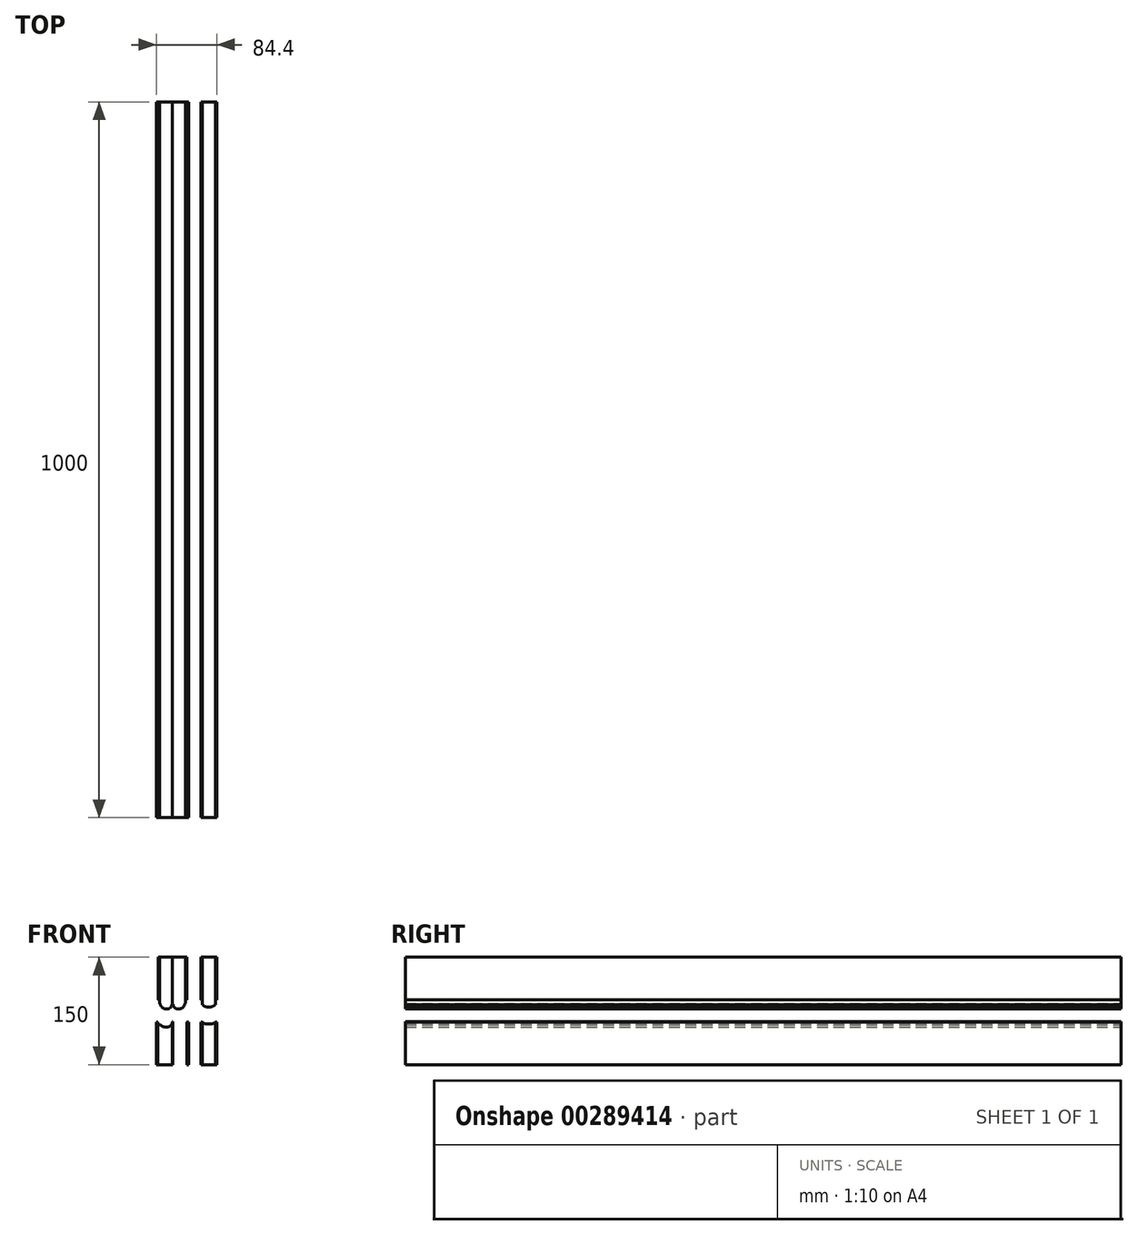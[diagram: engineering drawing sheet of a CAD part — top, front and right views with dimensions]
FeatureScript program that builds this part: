
annotation { "Feature Type Name" : "Feature", "Feature Type Description" : "" }
export const myFeature = defineFeature(function(context is Context, id is Id, definition is map)
    precondition{}
    {
        {
            assignVariable(context, id + "F0", {"name" : "lProfil", "anyValue" : 1000});
        }
        {
            var Q0;
            Q0=qCreatedBy(makeId("Front.planeOp"),FACE);
            var sketch = newSketch(context, id + "F1", { "sketchPlane" : qUnion([Q0])});
            skLineSegment(sketch, "E0.bottom", {"start": v(-18, 72.21) * mm, "end": v(0, 72.21) * mm});
            skLineSegment(sketch, "E0.top", {"start": v(-9.3, 0) * mm, "end": v(-7.3, 0) * mm});
            skLineSegment(sketch, "E0.left", {"start": v(-18, 72.21) * mm, "end": v(-18, 8) * mm});
            skLineSegment(sketch, "E0.right", {"start": v(0, 72.21) * mm, "end": v(0, 6.3) * mm});
            skPoint(sketch, "E1.visualSharp", {"position": v(0, 0) * mm});
            skArc(sketch, "E1.filletArc", {"start": v(-7.3, 0) * mm, "mid": v(-2.85, 1.85) * mm, "end": v(-1, 6.3) * mm});
            skPoint(sketch, "E2.visualSharp", {"position": v(-18, 0) * mm});
            skArc(sketch, "E2.filletArc", {"start": v(-17.3, 8) * mm, "mid": v(-14.96, 2.34) * mm, "end": v(-9.3, 0) * mm});
            skLineSegment(sketch, "E3", {"start": v(0, 6.3) * mm, "end": v(-1, 6.3) * mm});
            skLineSegment(sketch, "E4", {"start": v(-18, 8) * mm, "end": v(-17.3, 8) * mm});
            skLineSegment(sketch, "E5.MirrorCS", {"start": v(18, 72.21) * mm, "end": v(0, 72.21) * mm});
            skLineSegment(sketch, "E6.MirrorCS", {"start": v(18, 72.21) * mm, "end": v(18, 8) * mm});
            skLineSegment(sketch, "E7.MirrorCS", {"start": v(18, 8) * mm, "end": v(17.3, 8) * mm});
            skArc(sketch, "E8.MirrorCS", {"start": v(17.3, 8) * mm, "mid": v(14.96, 2.34) * mm, "end": v(9.3, 0) * mm});
            skLineSegment(sketch, "E9.MirrorCS", {"start": v(9.3, 0) * mm, "end": v(7.3, 0) * mm});
            skArc(sketch, "E10.MirrorCS", {"start": v(7.3, 0) * mm, "mid": v(2.85, 1.85) * mm, "end": v(1, 6.3) * mm});
            skLineSegment(sketch, "E11.MirrorCS", {"start": v(0, 6.3) * mm, "end": v(1, 6.3) * mm});
            skLineSegment(sketch, "E12.bottom", {"start": v(-0.4, -17.79) * mm, "end": v(0.4, -17.79) * mm});
            skLineSegment(sketch, "E12.top", {"start": v(-0.4, -77.79) * mm, "end": v(0.4, -77.79) * mm});
            skLineSegment(sketch, "E12.left", {"start": v(-0.4, -17.79) * mm, "end": v(-0.4, -77.79) * mm});
            skLineSegment(sketch, "E12.right", {"start": v(0.4, -17.79) * mm, "end": v(0.4, -77.79) * mm});
            skLineSegment(sketch, "E13", {"start": v(0, 0) * mm, "end": v(0, 6.3) * mm, "construction": true});
            skLineSegment(sketch, "E14", {"start": v(-10.7, -25.09) * mm, "end": v(-6.7, -25.09) * mm});
            skArc(sketch, "E15", {"start": v(-6.7, -25.09) * mm, "mid": v(-2.25, -23.24) * mm, "end": v(-0.4, -18.79) * mm});
            skArc(sketch, "E16", {"start": v(-10.7, -25.09) * mm, "mid": v(-13.96, -24.4) * mm, "end": v(-16.66, -22.43) * mm});
            skLineSegment(sketch, "E17", {"start": v(-16.66, -22.43) * mm, "end": v(-20.4, -22.43) * mm});
            skLineSegment(sketch, "E18", {"start": v(-20.4, -77.79) * mm, "end": v(-0.4, -77.79) * mm});
            skLineSegment(sketch, "E19", {"start": v(-18, 8) * mm, "end": v(-16.66, 4.86) * mm, "construction": true});
            skArc(sketch, "E20.MirrorCS", {"start": v(6.7, -25.09) * mm, "mid": v(2.25, -23.24) * mm, "end": v(0.4, -18.79) * mm});
            skLineSegment(sketch, "E21.MirrorCS", {"start": v(10.7, -25.09) * mm, "end": v(6.7, -25.09) * mm});
            skArc(sketch, "E22.MirrorCS", {"start": v(10.7, -25.09) * mm, "mid": v(13.96, -24.4) * mm, "end": v(16.66, -22.43) * mm});
            skLineSegment(sketch, "E23.MirrorCS", {"start": v(16.66, -22.43) * mm, "end": v(20.4, -22.43) * mm});
            skLineSegment(sketch, "E24.MirrorCS", {"start": v(20.4, -22.43) * mm, "end": v(20.4, -77.79) * mm});
            skLineSegment(sketch, "E25.MirrorCS", {"start": v(20.4, -77.79) * mm, "end": v(0.4, -77.79) * mm});
            skLineSegment(sketch, "E26.bottom", {"start": v(-20.4, -77.79) * mm, "end": v(-22.4, -77.79) * mm});
            skLineSegment(sketch, "E26.top", {"start": v(-20.9, -18.25) * mm, "end": v(-22.4, -18.25) * mm});
            skLineSegment(sketch, "E26.left", {"start": v(-20.4, -77.79) * mm, "end": v(-20.4, -18.75) * mm});
            skLineSegment(sketch, "E26.right", {"start": v(-22.4, -77.79) * mm, "end": v(-22.4, -18.25) * mm});
            skLineSegment(sketch, "E27", {"start": v(-20.4, -18.25) * mm, "end": v(-16.66, -22.43) * mm, "construction": true});
            skPoint(sketch, "E28.visualSharp", {"position": v(-20.4, -18.25) * mm});
            skArc(sketch, "E28.filletArc", {"start": v(-20.4, -18.75) * mm, "mid": v(-20.55, -18.4) * mm, "end": v(-20.9, -18.25) * mm});
            skLineSegment(sketch, "E29.MirrorCS", {"start": v(22.4, -77.79) * mm, "end": v(22.4, -18.25) * mm});
            skLineSegment(sketch, "E30.MirrorCS", {"start": v(20.4, -77.79) * mm, "end": v(22.4, -77.79) * mm});
            skLineSegment(sketch, "E31.MirrorCS", {"start": v(20.9, -18.25) * mm, "end": v(22.4, -18.25) * mm});
            skLineSegment(sketch, "E32.MirrorCS", {"start": v(20.4, -77.79) * mm, "end": v(20.4, -18.75) * mm});
            skArc(sketch, "E33.MirrorCS", {"start": v(20.4, -18.75) * mm, "mid": v(20.55, -18.4) * mm, "end": v(20.9, -18.25) * mm});
            skLineSegment(sketch, "E34.bottom", {"start": v(-18, 72.21) * mm, "end": v(-20, 72.21) * mm});
            skLineSegment(sketch, "E34.top", {"start": v(-18, 12.68) * mm, "end": v(-19.5, 12.68) * mm});
            skLineSegment(sketch, "E34.right", {"start": v(-20, 72.21) * mm, "end": v(-20, 13.18) * mm});
            skPoint(sketch, "E35.visualSharp", {"position": v(-20, 12.68) * mm});
            skArc(sketch, "E35.filletArc", {"start": v(-20, 13.18) * mm, "mid": v(-19.85, 12.83) * mm, "end": v(-19.5, 12.68) * mm});
            skLineSegment(sketch, "E36.MirrorCS", {"start": v(18, 12.68) * mm, "end": v(19.5, 12.68) * mm});
            skArc(sketch, "E37.MirrorCS", {"start": v(20, 13.18) * mm, "mid": v(19.85, 12.83) * mm, "end": v(19.5, 12.68) * mm});
            skLineSegment(sketch, "E38.MirrorCS", {"start": v(20, 72.21) * mm, "end": v(20, 13.18) * mm});
            skLineSegment(sketch, "E39.MirrorCS", {"start": v(18, 72.21) * mm, "end": v(20, 72.21) * mm});
            skLineSegment(sketch, "E40.bottom", {"start": v(42, 72.21) * mm, "end": v(60, 72.21) * mm});
            skLineSegment(sketch, "E40.left", {"start": v(42, 72.21) * mm, "end": v(42, 6) * mm});
            skLineSegment(sketch, "E40.right", {"start": v(60, 72.21) * mm, "end": v(60, 6.08) * mm});
            skLineSegment(sketch, "E41", {"start": v(49.28, 2.62) * mm, "end": v(51.28, 2.62) * mm});
            skArc(sketch, "E42", {"start": v(51.28, 2.62) * mm, "mid": v(55.97, 3.52) * mm, "end": v(60, 6.08) * mm});
            skArc(sketch, "E43", {"start": v(49.28, 2.62) * mm, "mid": v(45.27, 3.5) * mm, "end": v(42, 6) * mm});
            skLineSegment(sketch, "E44", {"start": v(30, 72.21) * mm, "end": v(30, 0) * mm, "construction": true});
            skLineSegment(sketch, "E45.MirrorCS", {"start": v(40, 72.21) * mm, "end": v(40, 13.18) * mm});
            skLineSegment(sketch, "E46.MirrorCS", {"start": v(42, 12.68) * mm, "end": v(40.5, 12.68) * mm});
            skArc(sketch, "E47.MirrorCS", {"start": v(40, 13.18) * mm, "mid": v(40.15, 12.83) * mm, "end": v(40.5, 12.68) * mm});
            skLineSegment(sketch, "E48.MirrorCS", {"start": v(42, 72.21) * mm, "end": v(40, 72.21) * mm});
            skLineSegment(sketch, "E49", {"start": v(51, 72.21) * mm, "end": v(51, 2.62) * mm, "construction": true});
            skLineSegment(sketch, "E50.MirrorCS", {"start": v(62, 72.21) * mm, "end": v(62, 13.18) * mm});
            skLineSegment(sketch, "E51.MirrorCS", {"start": v(60, 12.68) * mm, "end": v(61.5, 12.68) * mm});
            skArc(sketch, "E52.MirrorCS", {"start": v(62, 13.18) * mm, "mid": v(61.85, 12.83) * mm, "end": v(61.5, 12.68) * mm});
            skLineSegment(sketch, "E53.MirrorCS", {"start": v(60, 72.21) * mm, "end": v(62, 72.21) * mm});
            skLineSegment(sketch, "E54.MirrorCS", {"start": v(42, -77.79) * mm, "end": v(42, -18.75) * mm});
            skLineSegment(sketch, "E55.MirrorCS", {"start": v(40, -77.79) * mm, "end": v(40, -18.25) * mm});
            skLineSegment(sketch, "E56.MirrorCS", {"start": v(41.5, -18.25) * mm, "end": v(40, -18.25) * mm});
            skArc(sketch, "E57.MirrorCS", {"start": v(42, -18.75) * mm, "mid": v(41.85, -18.4) * mm, "end": v(41.5, -18.25) * mm});
            skLineSegment(sketch, "E58.MirrorCS", {"start": v(42, -77.79) * mm, "end": v(40, -77.79) * mm});
            skLineSegment(sketch, "E59.MirrorCS", {"start": v(60, -77.79) * mm, "end": v(60, -18.75) * mm});
            skLineSegment(sketch, "E60.MirrorCS", {"start": v(62, -77.79) * mm, "end": v(62, -18.25) * mm});
            skLineSegment(sketch, "E61.MirrorCS", {"start": v(60.5, -18.25) * mm, "end": v(62, -18.25) * mm});
            skArc(sketch, "E62.MirrorCS", {"start": v(60, -18.75) * mm, "mid": v(60.15, -18.4) * mm, "end": v(60.5, -18.25) * mm});
            skLineSegment(sketch, "E63.MirrorCS", {"start": v(60, -77.79) * mm, "end": v(62, -77.79) * mm});
            skLineSegment(sketch, "E64", {"start": v(42, -77.79) * mm, "end": v(60, -77.79) * mm});
            skLineSegment(sketch, "E65", {"start": v(48.28, -21.12) * mm, "end": v(52.28, -21.12) * mm});
            skArc(sketch, "E66", {"start": v(52.28, -21.12) * mm, "mid": v(56.16, -20.51) * mm, "end": v(59.67, -18.75) * mm});
            skArc(sketch, "E67", {"start": v(48.28, -21.12) * mm, "mid": v(44.93, -20.5) * mm, "end": v(42, -18.75) * mm});
            skLineSegment(sketch, "E68", {"start": v(50.28, 2.62) * mm, "end": v(50.28, -21.12) * mm, "construction": true});
            skLineSegment(sketch, "E69", {"start": v(60, -18.75) * mm, "end": v(59.67, -18.75) * mm});
            skSolve(sketch);
        }
        {
            var Q0;
            Q0=makeQuery(id+"F1.imprint","IMPRINT",FACE,{"disambiguationData":[TD([[makeQuery(id+"F1.imprint","IMPRINT",EDGE,{"derivedFrom":sQuery(id+"F1.wireOp",EDGE,"E0.bottom")}),-1.0]])]});
            var Q1;
            Q1=makeQuery(id+"F1.imprint","IMPRINT",FACE,{"disambiguationData":[TD([[makeQuery(id+"F1.imprint","IMPRINT",EDGE,{"derivedFrom":sQuery(id+"F1.wireOp",EDGE,"E14")}),-1.0]])]});
            var Q2;
            {var subQ1=sQuery(id+"F1.wireOp",EDGE,"E40.bottom");Q2=makeQuery(id+"F1.imprint","IMPRINT",FACE,{"disambiguationData":[TD([[makeQuery(id+"F1.imprint","IMPRINT",EDGE,{"derivedFrom":subQ1}),-1.0]])]});}
            var Q3;
            Q3=makeQuery(id+"F1.imprint","IMPRINT",FACE,{"disambiguationData":[TD([[makeQuery(id+"F1.imprint","IMPRINT",EDGE,{"derivedFrom":sQuery(id+"F1.wireOp",EDGE,"E54.MirrorCS")}),-1.0]])]});
            extrude(context, id + "F2", {"entities" : qUnion([Q0, Q1, Q2, Q3]), "depth" : (getVariable(context, 'lProfil')) * mm});
        }
        {
            var Q0;
            {var subQ0=sQuery(id+"F1.wireOp",EDGE,"E20.MirrorCS");Q0=makeQuery(id+"F1.imprint","IMPRINT",FACE,{"disambiguationData":[TD([[makeQuery(id+"F1.imprint","IMPRINT",EDGE,{"derivedFrom":subQ0}),1.0]])]});}
            var Q1;
            Q1=makeQuery(id+"F1.imprint","IMPRINT",FACE,{"disambiguationData":[TD([[makeQuery(id+"F1.imprint","IMPRINT",EDGE,{"derivedFrom":sQuery(id+"F1.wireOp",EDGE,"E0.right")}),1.0]])]});
            extrude(context, id + "F3", {"entities" : qUnion([Q0, Q1]), "depth" : (getVariable(context, 'lProfil')) * mm});
        }
        {
            var Q0;
            {var subQ3=sQuery(id+"F1.wireOp",EDGE,"E26.bottom");Q0=makeQuery(id+"F1.imprint","IMPRINT",FACE,{"disambiguationData":[TD([[makeQuery(id+"F1.imprint","IMPRINT",EDGE,{"derivedFrom":subQ3}),-1.0]])]});}
            var Q1;
            {var subQ3=sQuery(id+"F1.wireOp",EDGE,"E12.bottom");Q1=makeQuery(id+"F1.imprint","IMPRINT",FACE,{"disambiguationData":[TD([[makeQuery(id+"F1.imprint","IMPRINT",EDGE,{"derivedFrom":subQ3}),-1.0]])]});}
            var Q2;
            Q2=makeQuery(id+"F1.imprint","IMPRINT",FACE,{"disambiguationData":[TD([[makeQuery(id+"F1.imprint","IMPRINT",EDGE,{"derivedFrom":sQuery(id+"F1.wireOp",EDGE,"E29.MirrorCS")}),1.0]])]});
            var Q3;
            {var subQ1=sQuery(id+"F1.wireOp",EDGE,"E34.bottom");Q3=makeQuery(id+"F1.imprint","IMPRINT",FACE,{"disambiguationData":[TD([[makeQuery(id+"F1.imprint","IMPRINT",EDGE,{"derivedFrom":subQ1}),1.0]])]});}
            var Q4;
            {var subQ0=sQuery(id+"F1.wireOp",EDGE,"E36.MirrorCS");Q4=makeQuery(id+"F1.imprint","IMPRINT",FACE,{"disambiguationData":[TD([[makeQuery(id+"F1.imprint","IMPRINT",EDGE,{"derivedFrom":subQ0}),1.0]])]});}
            var Q5;
            Q5=makeQuery(id+"F1.imprint","IMPRINT",FACE,{"disambiguationData":[TD([[makeQuery(id+"F1.imprint","IMPRINT",EDGE,{"derivedFrom":sQuery(id+"F1.wireOp",EDGE,"E50.MirrorCS")}),-1.0]])]});
            var Q6;
            Q6=makeQuery(id+"F1.imprint","IMPRINT",FACE,{"disambiguationData":[TD([[makeQuery(id+"F1.imprint","IMPRINT",EDGE,{"derivedFrom":sQuery(id+"F1.wireOp",EDGE,"E45.MirrorCS")}),1.0]])]});
            var Q7;
            Q7=makeQuery(id+"F1.imprint","IMPRINT",FACE,{"disambiguationData":[TD([[makeQuery(id+"F1.imprint","IMPRINT",EDGE,{"derivedFrom":sQuery(id+"F1.wireOp",EDGE,"E54.MirrorCS")}),1.0]])]});
            var Q8;
            Q8=makeQuery(id+"F1.imprint","IMPRINT",FACE,{"disambiguationData":[TD([[makeQuery(id+"F1.imprint","IMPRINT",EDGE,{"derivedFrom":sQuery(id+"F1.wireOp",EDGE,"E59.MirrorCS")}),-1.0]])]});
            extrude(context, id + "F4", {"entities" : qUnion([Q0, Q1, Q2, Q3, Q4, Q5, Q6, Q7, Q8]), "depth" : (getVariable(context, 'lProfil')) * mm});
        }
    });
